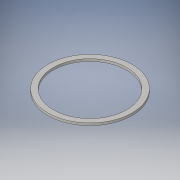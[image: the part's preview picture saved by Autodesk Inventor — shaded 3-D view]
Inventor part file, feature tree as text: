
AUTODESK INVENTOR PART (.ipt)
format: ipt  version: 2016 (Build 200138000, 138)  size: 97,280 bytes
history: native  units: in
note: dims shown in document units (in); Inventor stores cm internally (conversion verified against a paired STEP export)
features: extrude x1, sketch x1
ambient origin geometry x8: Origin, YZ Plane, XZ Plane, XY Plane, X Axis, Y Axis, Z Axis, Center Point
bodies: Solid1 (feature_tree)
feature tree (2):
  extrude  "Extrusion1"  Depth=0.11in
  sketch  "Sketch1"  dims[d0=0.25in d1=3.44in d2=0.11in d3=0.0in]
